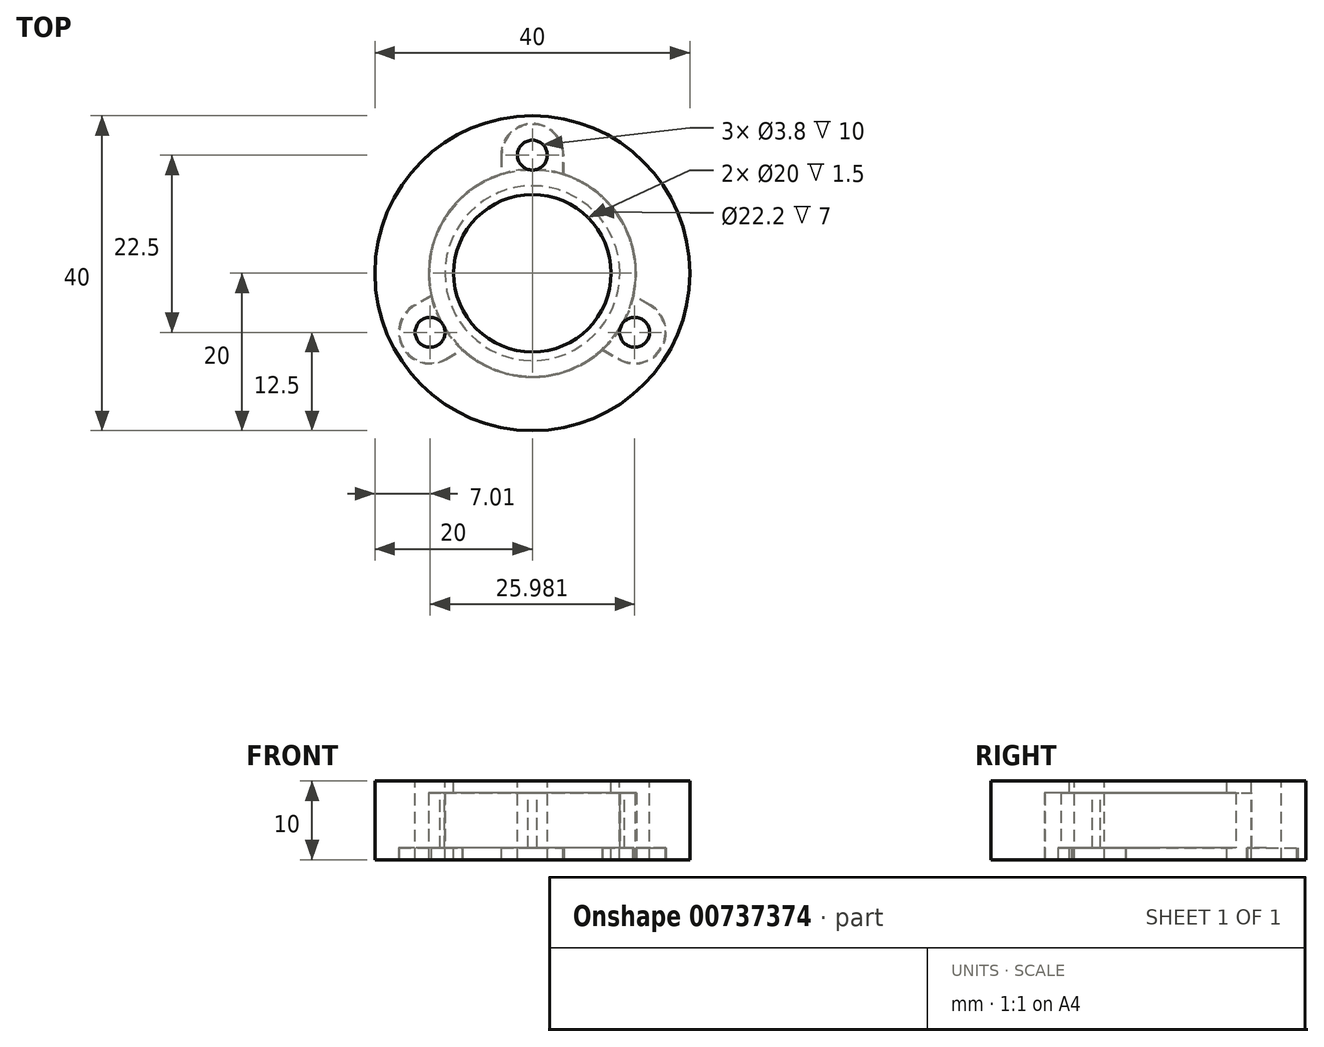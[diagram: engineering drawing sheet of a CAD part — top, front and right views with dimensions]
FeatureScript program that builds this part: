
annotation { "Feature Type Name" : "Feature", "Feature Type Description" : "" }
export const myFeature = defineFeature(function(context is Context, id is Id, definition is map)
    precondition{}
    {
        {
            var Q0;
            Q0=qCreatedBy(makeId("Top.planeOp"),FACE);
            var sketch = newSketch(context, id + "F0", { "sketchPlane" : qUnion([Q0])});
            skCircle(sketch, "E0", {"center": v(0, 0) * mm, "radius": 11.1 * mm, "construction": true});
            skArc(sketch, "E1", {"start": v(-3.9, 12.5) * mm, "mid": v(-11.34, 6.55) * mm, "end": v(-12.78, -2.88) * mm});
            skCircle(sketch, "E2", {"center": v(0, 15) * mm, "radius": 1.9 * mm});
            skArc(sketch, "E3", {"start": v(3.9, 15) * mm, "mid": v(0, 18.9) * mm, "end": v(-3.9, 15) * mm});
            skLineSegment(sketch, "E4", {"start": v(-3.9, 15) * mm, "end": v(-3.9, 12.5) * mm});
            skLineSegment(sketch, "E5", {"start": v(3.9, 12.5) * mm, "end": v(3.9, 15) * mm});
            skCircle(sketch, "E6.1.0", {"center": v(-13, -7.5) * mm, "radius": 1.9 * mm});
            skLineSegment(sketch, "E6.1.1", {"start": v(-11.04, -10.88) * mm, "end": v(-8.88, -9.63) * mm});
            skArc(sketch, "E6.1.2", {"start": v(-14.94, -4.12) * mm, "mid": v(-16.37, -9.45) * mm, "end": v(-11.04, -10.88) * mm});
            skLineSegment(sketch, "E6.1.3", {"start": v(-12.78, -2.88) * mm, "end": v(-14.94, -4.12) * mm});
            skCircle(sketch, "E6.2.0", {"center": v(13, -7.5) * mm, "radius": 1.9 * mm});
            skLineSegment(sketch, "E6.2.1", {"start": v(14.94, -4.12) * mm, "end": v(12.78, -2.88) * mm});
            skArc(sketch, "E6.2.2", {"start": v(11.04, -10.88) * mm, "mid": v(16.37, -9.45) * mm, "end": v(14.94, -4.12) * mm});
            skLineSegment(sketch, "E6.2.3", {"start": v(8.88, -9.63) * mm, "end": v(11.04, -10.88) * mm});
            skArc(sketch, "E7.trimOffspring", {"start": v(-8.88, -9.63) * mm, "mid": v(0, -13.1) * mm, "end": v(8.88, -9.63) * mm});
            skArc(sketch, "E8.trimOffspring", {"start": v(12.78, -2.88) * mm, "mid": v(11.34, 6.55) * mm, "end": v(3.9, 12.5) * mm});
            skCircle(sketch, "E9", {"center": v(0, 0) * mm, "radius": 10 * mm});
            skSolve(sketch);
        }
        {
            var Q0;
            Q0 = qSketchRegion(id + "F0", true);
            extrude(context, id + "F1", {"entities" : qUnion([Q0]), "oppositeDirection" : true, "depth" : 1.5 * mm, "offsetDistance" : 25 * mm});
        }
        {
            var Q0;
            Q0=makeQuery(id+"F1.opExtrude","CAP_FACE",FACE,{"disambiguationData":[OSD([sQuery(id+"F0.wireOp",EDGE,"E1"),sQuery(id+"F0.wireOp",EDGE,"E2"),sQuery(id+"F0.wireOp",EDGE,"E3"),sQuery(id+"F0.wireOp",EDGE,"E4"),sQuery(id+"F0.wireOp",EDGE,"E5"),sQuery(id+"F0.wireOp",EDGE,"E6.1.0"),sQuery(id+"F0.wireOp",EDGE,"E6.1.1"),sQuery(id+"F0.wireOp",EDGE,"E6.1.2"),sQuery(id+"F0.wireOp",EDGE,"E6.1.3"),sQuery(id+"F0.wireOp",EDGE,"E6.2.0"),sQuery(id+"F0.wireOp",EDGE,"E6.2.1"),sQuery(id+"F0.wireOp",EDGE,"E6.2.2"),sQuery(id+"F0.wireOp",EDGE,"E6.2.3"),sQuery(id+"F0.wireOp",EDGE,"E7.trimOffspring"),sQuery(id+"F0.wireOp",EDGE,"E8.trimOffspring"),sQuery(id+"F0.wireOp",EDGE,"E9")])],"isStart":true});
            var sketch = newSketch(context, id + "F2", { "sketchPlane" : qUnion([Q0])});
            skCircle(sketch, "E10", {"center": v(0, 0) * mm, "radius": 11.1 * mm});
            skCircle(sketch, "E11", {"center": v(0, 0) * mm, "radius": 13.1 * mm});
            skSolve(sketch);
        }
        {
            var Q0;
            Q0 = qSketchRegion(id + "F2", true);
            extrude(context, id + "F3", {"entities" : qUnion([Q0]), "operationType" : NewBodyOperationType.ADD, "depth" : 7 * mm, "offsetDistance" : 25 * mm});
        }
        {
            var Q0;
            Q0=makeQuery(id+"F1.opExtrude","CAP_FACE",FACE,{"disambiguationData":[OSD([sQuery(id+"F0.wireOp",EDGE,"E1"),sQuery(id+"F0.wireOp",EDGE,"E2"),sQuery(id+"F0.wireOp",EDGE,"E3"),sQuery(id+"F0.wireOp",EDGE,"E4"),sQuery(id+"F0.wireOp",EDGE,"E5"),sQuery(id+"F0.wireOp",EDGE,"E6.1.0"),sQuery(id+"F0.wireOp",EDGE,"E6.1.1"),sQuery(id+"F0.wireOp",EDGE,"E6.1.2"),sQuery(id+"F0.wireOp",EDGE,"E6.1.3"),sQuery(id+"F0.wireOp",EDGE,"E6.2.0"),sQuery(id+"F0.wireOp",EDGE,"E6.2.1"),sQuery(id+"F0.wireOp",EDGE,"E6.2.2"),sQuery(id+"F0.wireOp",EDGE,"E6.2.3"),sQuery(id+"F0.wireOp",EDGE,"E7.trimOffspring"),sQuery(id+"F0.wireOp",EDGE,"E8.trimOffspring"),sQuery(id+"F0.wireOp",EDGE,"E9")])],"isStart":false});
            var sketch = newSketch(context, id + "F4", { "sketchPlane" : qUnion([Q0])});
            skCircle(sketch, "E12", {"center": v(0, 0) * mm, "radius": 20 * mm});
            skCircle(sketch, "E13", {"center": v(0, 0) * mm, "radius": 13.2 * mm});
            skLineSegment(sketch, "E14.0", {"start": v(-4, -15) * mm, "end": v(-4, -12.58) * mm});
            skArc(sketch, "E14.1", {"start": v(4, -15) * mm, "mid": v(0, -19) * mm, "end": v(-4, -15) * mm});
            skLineSegment(sketch, "E14.2", {"start": v(4, -12.58) * mm, "end": v(4, -15) * mm});
            skLineSegment(sketch, "E15.1.0", {"start": v(15, 4.04) * mm, "end": v(12.9, 2.83) * mm});
            skArc(sketch, "E15.1.1", {"start": v(11, 10.96) * mm, "mid": v(16.45, 9.5) * mm, "end": v(15, 4.04) * mm});
            skLineSegment(sketch, "E15.1.2", {"start": v(8.9, 9.75) * mm, "end": v(11, 10.96) * mm});
            skLineSegment(sketch, "E15.2.0", {"start": v(-11, 10.96) * mm, "end": v(-8.9, 9.75) * mm});
            skArc(sketch, "E15.2.1", {"start": v(-15, 4.04) * mm, "mid": v(-16.45, 9.5) * mm, "end": v(-11, 10.96) * mm});
            skLineSegment(sketch, "E15.2.2", {"start": v(-12.9, 2.83) * mm, "end": v(-15, 4.04) * mm});
            skSolve(sketch);
        }
        {
            var Q0;
            Q0 = qSketchRegion(id + "F4", true);
            extrude(context, id + "F5", {"entities" : qUnion([Q0]), "oppositeDirection" : true, "depth" : 10 * mm, "offsetDistance" : 25 * mm});
        }
        {
            var Q0;
            Q0=makeQuery(id+"F5.opExtrude","CAP_FACE",FACE,{"disambiguationData":[OSD([sQuery(id+"F4.wireOp",EDGE,"E12"),sQuery(id+"F4.wireOp",EDGE,"E13"),sQuery(id+"F4.wireOp",EDGE,"E14.0"),sQuery(id+"F4.wireOp",EDGE,"E14.1"),sQuery(id+"F4.wireOp",EDGE,"E14.2"),sQuery(id+"F4.wireOp",EDGE,"E15.1.0"),sQuery(id+"F4.wireOp",EDGE,"E15.1.1"),sQuery(id+"F4.wireOp",EDGE,"E15.1.2"),sQuery(id+"F4.wireOp",EDGE,"E15.2.0"),sQuery(id+"F4.wireOp",EDGE,"E15.2.1"),sQuery(id+"F4.wireOp",EDGE,"E15.2.2")])],"isStart":false});
            var sketch = newSketch(context, id + "F6", { "sketchPlane" : qUnion([Q0])});
            skCircle(sketch, "E16", {"center": v(0, 0) * mm, "radius": 10 * mm});
            skCircle(sketch, "E17.0", {"center": v(-13, -7.5) * mm, "radius": 1.9 * mm});
            skCircle(sketch, "E17.1", {"center": v(13, -7.5) * mm, "radius": 1.9 * mm});
            skCircle(sketch, "E17.2", {"center": v(0, 15) * mm, "radius": 1.9 * mm});
            skCircle(sketch, "E18", {"center": v(0, 0) * mm, "radius": 19.42 * mm});
            skSolve(sketch);
        }
        {
            var Q0;
            Q0 = qSketchRegion(id + "F6", true);
            extrude(context, id + "F7", {"entities" : qUnion([Q0]), "operationType" : NewBodyOperationType.ADD, "oppositeDirection" : true, "depth" : 1.5 * mm, "offsetDistance" : 25 * mm});
        }
        {
            var Q0;
            Q0=makeQuery(id+"F7.opExtrude","CAP_FACE",FACE,{"disambiguationData":[OSD([sQuery(id+"F6.wireOp",EDGE,"E16"),sQuery(id+"F6.wireOp",EDGE,"E17.0"),sQuery(id+"F6.wireOp",EDGE,"E17.1"),sQuery(id+"F6.wireOp",EDGE,"E17.2"),sQuery(id+"F6.wireOp",EDGE,"E18")])],"isStart":false});
            var sketch = newSketch(context, id + "F8", { "sketchPlane" : qUnion([Q0])});
            skLineSegment(sketch, "E19.0", {"start": v(-12.9, 2.83) * mm, "end": v(-15, 4.04) * mm});
            skArc(sketch, "E19.1", {"start": v(-15, 4.04) * mm, "mid": v(-16.45, 9.5) * mm, "end": v(-11, 10.96) * mm});
            skLineSegment(sketch, "E19.2", {"start": v(-11, 10.96) * mm, "end": v(-8.9, 9.75) * mm});
            skArc(sketch, "E20.0", {"start": v(-11.14, 7.09) * mm, "mid": v(-14.64, 8.45) * mm, "end": v(-11.7, 6.1) * mm});
            skArc(sketch, "E21", {"start": v(-8.9, 9.75) * mm, "mid": v(-10.1, 8.5) * mm, "end": v(-11.14, 7.09) * mm});
            skArc(sketch, "E22.trimOffspring", {"start": v(-11.7, 6.1) * mm, "mid": v(-12.4, 4.5) * mm, "end": v(-12.9, 2.83) * mm});
            skArc(sketch, "E23.1.0", {"start": v(4, -15) * mm, "mid": v(0, -19) * mm, "end": v(-4, -15) * mm});
            skArc(sketch, "E23.1.1", {"start": v(-0.57, -13.19) * mm, "mid": v(0, -16.9) * mm, "end": v(0.57, -13.19) * mm});
            skArc(sketch, "E23.1.2", {"start": v(-4, -12.58) * mm, "mid": v(-2.3, -13) * mm, "end": v(-0.57, -13.19) * mm});
            skArc(sketch, "E23.1.3", {"start": v(0.57, -13.19) * mm, "mid": v(2.3, -13) * mm, "end": v(4, -12.58) * mm});
            skLineSegment(sketch, "E23.1.4", {"start": v(4, -12.58) * mm, "end": v(4, -15) * mm});
            skLineSegment(sketch, "E23.1.5", {"start": v(-4, -15) * mm, "end": v(-4, -12.58) * mm});
            skArc(sketch, "E23.2.0", {"start": v(11, 10.96) * mm, "mid": v(16.45, 9.5) * mm, "end": v(15, 4.04) * mm});
            skArc(sketch, "E23.2.1", {"start": v(11.7, 6.1) * mm, "mid": v(14.64, 8.45) * mm, "end": v(11.14, 7.09) * mm});
            skArc(sketch, "E23.2.2", {"start": v(12.9, 2.83) * mm, "mid": v(12.4, 4.5) * mm, "end": v(11.7, 6.1) * mm});
            skArc(sketch, "E23.2.3", {"start": v(11.14, 7.09) * mm, "mid": v(10.1, 8.5) * mm, "end": v(8.9, 9.75) * mm});
            skLineSegment(sketch, "E23.2.4", {"start": v(8.9, 9.75) * mm, "end": v(11, 10.96) * mm});
            skLineSegment(sketch, "E23.2.5", {"start": v(15, 4.04) * mm, "end": v(12.9, 2.83) * mm});
            skSolve(sketch);
        }
        {
            var Q0;
            Q0 = qSketchRegion(id + "F8", true);
            extrude(context, id + "F9", {"entities" : qUnion([Q0]), "operationType" : NewBodyOperationType.ADD, "depth" : 7 * mm, "offsetDistance" : 25 * mm});
        }
    });
